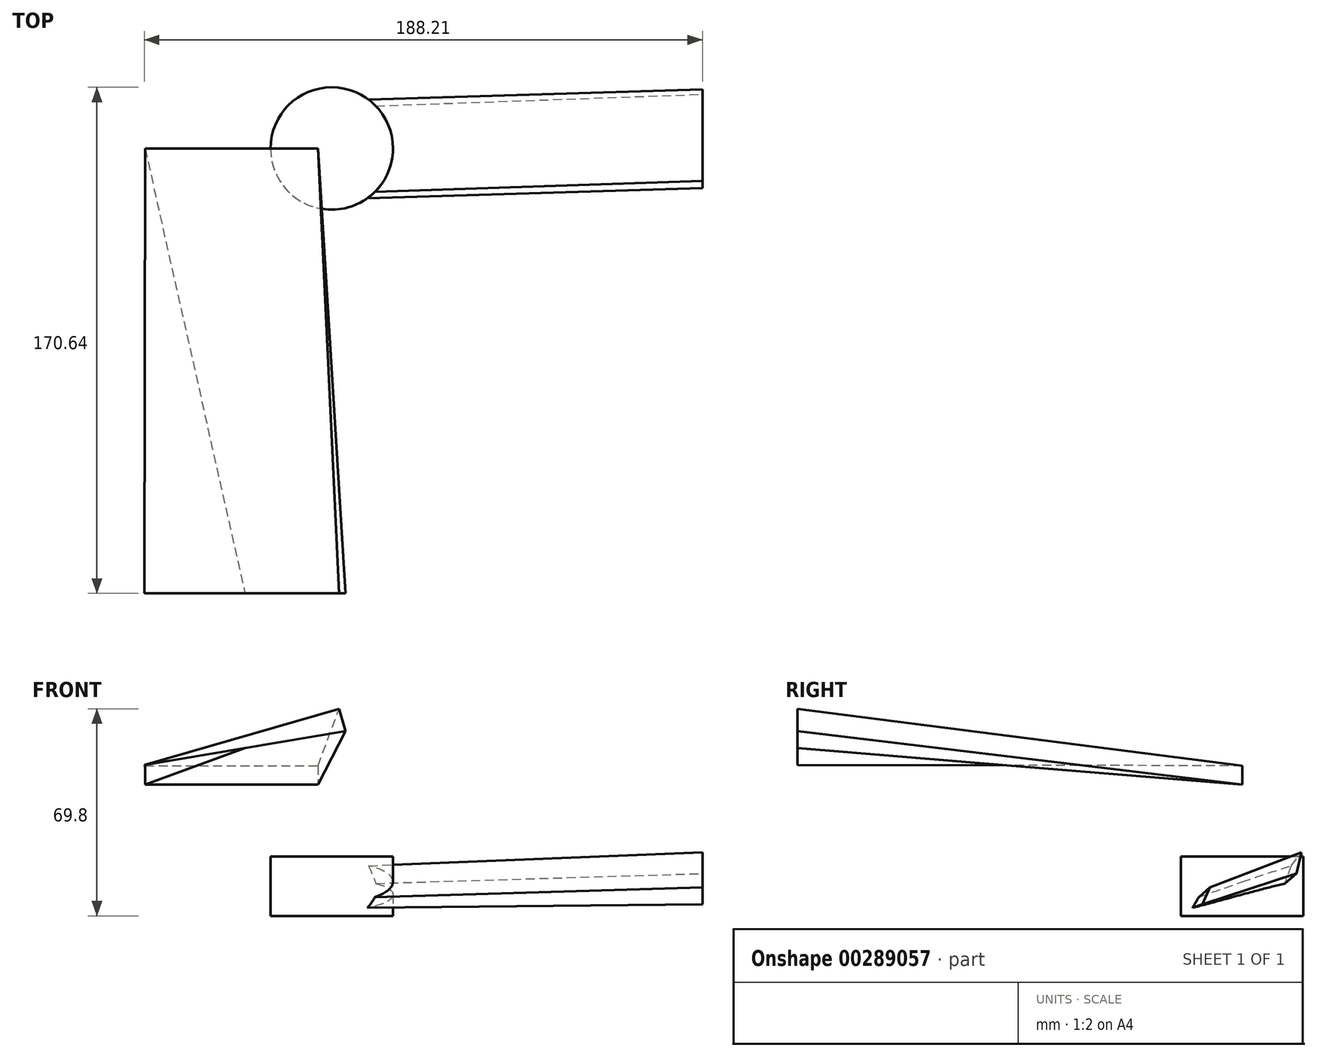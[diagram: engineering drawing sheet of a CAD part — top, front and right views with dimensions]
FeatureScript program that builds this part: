
annotation { "Feature Type Name" : "Feature", "Feature Type Description" : "" }
export const myFeature = defineFeature(function(context is Context, id is Id, definition is map)
    precondition{}
    {
        {
            var Q0;
            Q0=qCreatedBy(makeId("Top.planeOp"),FACE);
            var sketch = newSketch(context, id + "F0", { "sketchPlane" : qUnion([Q0])});
            skCircle(sketch, "E0", {"center": v(0, 0) * mm, "radius": 20.64 * mm});
            skSolve(sketch);
        }
        {
            var Q0;
            Q0=makeQuery(id+"F0.imprint","IMPRINT",FACE,{"disambiguationData":[TD([[makeQuery(id+"F0.imprint","IMPRINT",EDGE,{"derivedFrom":sQuery(id+"F0.wireOp",EDGE,"E0")}),1.0]])]});
            extrude(context, id + "F1", {"entities" : qUnion([Q0]), "depth" : 20 * mm});
        }
        {
            var Q0;
            Q0=qCreatedBy(makeId("Right.planeOp"),FACE);
            var sketch = newSketch(context, id + "F2", { "sketchPlane" : qUnion([Q0])});
            skLineSegment(sketch, "E1", {"start": v(-15.09, 5.88) * mm, "end": v(16.1, 16.36) * mm});
            skLineSegment(sketch, "E2", {"start": v(16.1, 16.36) * mm, "end": v(13.8, 10.48) * mm});
            skLineSegment(sketch, "E3", {"start": v(13.8, 10.48) * mm, "end": v(-17.13, 2.56) * mm});
            skLineSegment(sketch, "E4", {"start": v(-17.13, 2.56) * mm, "end": v(-15.09, 5.88) * mm});
            skSolve(sketch);
        }
        {
            var Q0;
            Q0=qCreatedBy(makeId("Right.planeOp"),FACE);
            cPlane(context, id + "F3", {"entities" : qUnion([Q0]), "cplaneType" : CPlaneType.OFFSET, "offset" : 125 * mm, "width" : 150 * mm, "height" : 150 * mm});
        }
        {
            var Q0;
            Q0=qCreatedBy(id+"F3.planeOp",FACE);
            var sketch = newSketch(context, id + "F4", { "sketchPlane" : qUnion([Q0])});
            skLineSegment(sketch, "E5", {"start": v(19.94, 21.48) * mm, "end": v(18.26, 14.26) * mm});
            skLineSegment(sketch, "E6", {"start": v(18.26, 14.26) * mm, "end": v(-13.37, 3.86) * mm});
            skLineSegment(sketch, "E7", {"start": v(-13.37, 3.86) * mm, "end": v(-10.93, 9.62) * mm});
            skLineSegment(sketch, "E8", {"start": v(-10.93, 9.62) * mm, "end": v(19.94, 21.48) * mm});
            skSolve(sketch);
        }
        {
            var Q1;
            Q1 = qSketchRegion(id + "F2", true);
            var Q2;
            Q2 = qSketchRegion(id + "F4", true);
            loft(context, id + "F5", {"operationType" : NewBodyOperationType.ADD, "sheetProfilesArray" : [{ "sheetProfileEntities" : qUnion([Q1]) }, { "sheetProfileEntities" : qUnion([Q2]) }]});
        }
        {
            var Q0;
            Q0=qCreatedBy(makeId("Front.planeOp"),FACE);
            var sketch = newSketch(context, id + "F6", { "sketchPlane" : qUnion([Q0])});
            skLineSegment(sketch, "E9.bottom", {"start": v(-62.95, 50.63) * mm, "end": v(-4.66, 50.63) * mm});
            skLineSegment(sketch, "E9.top", {"start": v(-62.95, 44.23) * mm, "end": v(-4.66, 44.23) * mm});
            skLineSegment(sketch, "E9.left", {"start": v(-62.95, 50.63) * mm, "end": v(-62.95, 44.23) * mm});
            skLineSegment(sketch, "E9.right", {"start": v(-4.66, 50.63) * mm, "end": v(-4.66, 44.23) * mm});
            skSolve(sketch);
        }
        {
            var Q0;
            Q0=qCreatedBy(makeId("Front.planeOp"),FACE);
            cPlane(context, id + "F7", {"entities" : qUnion([Q0]), "cplaneType" : CPlaneType.OFFSET, "offset" : 150 * mm, "width" : 150 * mm, "height" : 150 * mm});
        }
        {
            var Q0;
            Q0=qCreatedBy(id+"F7.planeOp",FACE);
            var sketch = newSketch(context, id + "F8", { "sketchPlane" : qUnion([Q0])});
            skLineSegment(sketch, "E10", {"start": v(-63.21, 50.88) * mm, "end": v(2.5, 69.8) * mm});
            skLineSegment(sketch, "E11", {"start": v(2.5, 69.8) * mm, "end": v(4.67, 62.27) * mm});
            skLineSegment(sketch, "E12", {"start": v(4.67, 62.27) * mm, "end": v(-63.21, 50.88) * mm});
            skSolve(sketch);
        }
        {
            var Q0;
            Q0=makeQuery(id+"F6.imprint","IMPRINT",FACE,{"disambiguationData":[TD([[makeQuery(id+"F6.imprint","IMPRINT",EDGE,{"derivedFrom":sQuery(id+"F6.wireOp",EDGE,"E9.bottom")}),-1.0]])]});
            var Q1;
            Q1=makeQuery(id+"F8.imprint","IMPRINT",FACE,{"disambiguationData":[TD([[makeQuery(id+"F8.imprint","IMPRINT",EDGE,{"derivedFrom":sQuery(id+"F8.wireOp",EDGE,"E10")}),-1.0]])]});
            loft(context, id + "F9", {"sheetProfilesArray" : [{ "sheetProfileEntities" : qUnion([Q0]) }, { "sheetProfileEntities" : qUnion([Q1]) }]});
        }
    });
